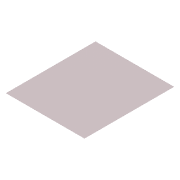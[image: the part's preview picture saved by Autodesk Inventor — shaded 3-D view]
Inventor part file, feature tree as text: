
AUTODESK INVENTOR PART (.ipt)
format: ipt  version: 2017 (Build 210142000, 142)  size: 87,040 bytes
history: native  units: in
note: dims shown in document units (in); Inventor stores cm internally (conversion verified against a paired STEP export)
features: extrude x1
ambient origin geometry x8: Origin, YZ Plane, XZ Plane, XY Plane, X Axis, Y Axis, Z Axis, Center Point
bodies: Solid1 (feature_tree)
feature tree (1):
  extrude  "Extrusion1"  Depth=28.5in
